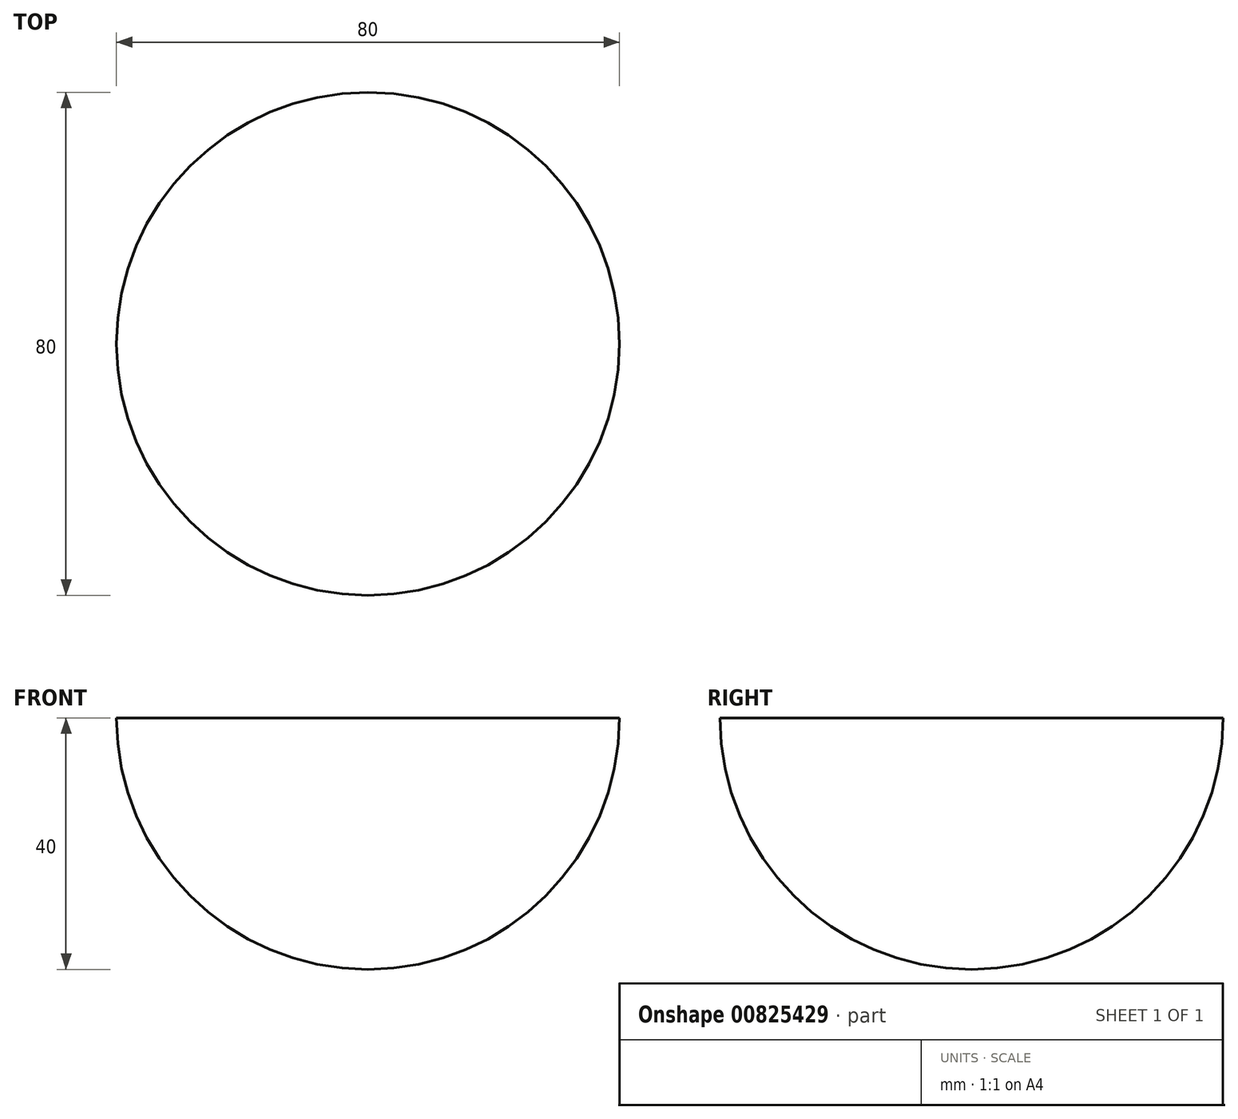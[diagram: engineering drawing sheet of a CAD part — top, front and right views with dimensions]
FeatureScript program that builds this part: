
annotation { "Feature Type Name" : "Feature", "Feature Type Description" : "" }
export const myFeature = defineFeature(function(context is Context, id is Id, definition is map)
    precondition{}
    {
        {
            var Q0;
            Q0=qCreatedBy(makeId("Top.planeOp"),FACE);
            var sketch = newSketch(context, id + "F0", { "sketchPlane" : qUnion([Q0])});
            skArc(sketch, "E0", {"start": v(0, 40) * mm, "mid": v(-40, 0) * mm, "end": v(0, -40) * mm});
            skLineSegment(sketch, "E1", {"start": v(0, 0) * mm, "end": v(0, 40) * mm});
            skLineSegment(sketch, "E2", {"start": v(0, 0) * mm, "end": v(0, -40) * mm});
            skSolve(sketch);
        }
        {
            var Q0;
            Q0=makeQuery(id+"F0.imprint","IMPRINT",FACE,{"disambiguationData":[TD([[makeQuery(id+"F0.imprint","IMPRINT",EDGE,{"derivedFrom":sQuery(id+"F0.wireOp",EDGE,"E0")}),1.0]])]});
            var Q1;
            Q1=sQuery(id+"F0.wireOp",EDGE,"E2");
            revolve(context, id + "F1", {"surfaceOperationType" : NewSurfaceOperationType.NEW, "entities" : qUnion([Q0]), "axis" : qUnion([Q1]), "revolveType" : RevolveType.ONE_DIRECTION, "angle" : 180 * degree});
        }
    });
